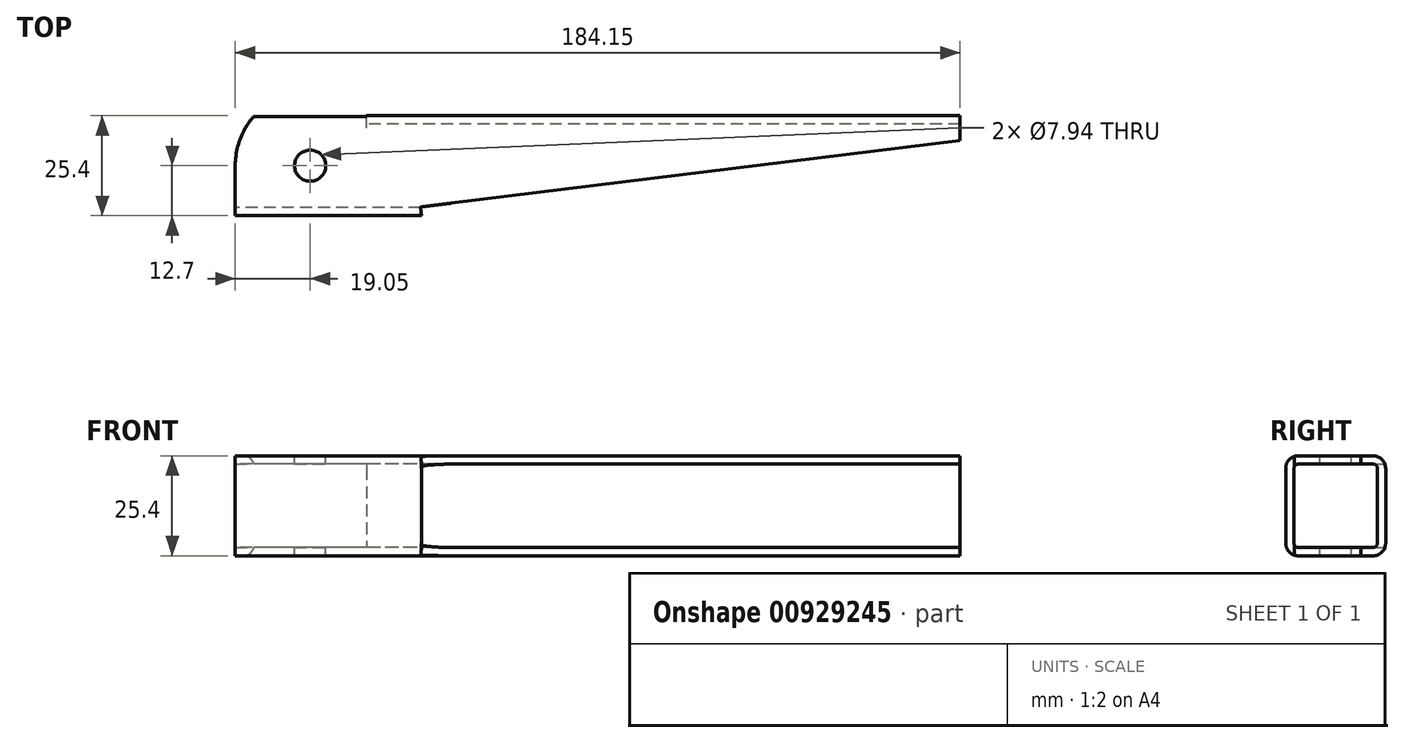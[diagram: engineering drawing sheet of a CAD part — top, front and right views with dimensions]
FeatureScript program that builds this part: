
annotation { "Feature Type Name" : "Feature", "Feature Type Description" : "" }
export const myFeature = defineFeature(function(context is Context, id is Id, definition is map)
    precondition{}
    {
        {
            var Q0;
            Q0=qCreatedBy(makeId("Right.planeOp"),FACE);
            var sketch = newSketch(context, id + "F0", { "sketchPlane" : qUnion([Q0])});
            skLineSegment(sketch, "E0.bottom", {"start": v(9.53, -12.7) * mm, "end": v(-9.53, -12.7) * mm});
            skLineSegment(sketch, "E0.top", {"start": v(9.53, 12.7) * mm, "end": v(-9.52, 12.7) * mm});
            skLineSegment(sketch, "E0.left", {"start": v(12.7, -9.53) * mm, "end": v(12.7, 9.53) * mm});
            skLineSegment(sketch, "E0.right", {"start": v(-12.7, -9.53) * mm, "end": v(-12.7, 9.52) * mm});
            skPoint(sketch, "E0.middle", {"position": v(0, 0) * mm});
            skPoint(sketch, "E1.visualSharp", {"position": v(-12.7, 12.7) * mm});
            skArc(sketch, "E1.filletArc", {"start": v(-9.52, 12.7) * mm, "mid": v(-11.77, 11.77) * mm, "end": v(-12.7, 9.52) * mm});
            skPoint(sketch, "E2.visualSharp", {"position": v(12.7, 12.7) * mm});
            skArc(sketch, "E2.filletArc", {"start": v(12.7, 9.53) * mm, "mid": v(11.77, 11.77) * mm, "end": v(9.53, 12.7) * mm});
            skPoint(sketch, "E3.visualSharp", {"position": v(12.7, -12.7) * mm});
            skArc(sketch, "E3.filletArc", {"start": v(9.53, -12.7) * mm, "mid": v(11.77, -11.77) * mm, "end": v(12.7, -9.53) * mm});
            skPoint(sketch, "E4.visualSharp", {"position": v(-12.7, -12.7) * mm});
            skArc(sketch, "E4.filletArc", {"start": v(-12.7, -9.53) * mm, "mid": v(-11.77, -11.77) * mm, "end": v(-9.53, -12.7) * mm});
            skLineSegment(sketch, "E5.0", {"start": v(9.53, 10.6) * mm, "end": v(-9.53, 10.6) * mm});
            skArc(sketch, "E5.1", {"start": v(10.6, 9.53) * mm, "mid": v(10.28, 10.28) * mm, "end": v(9.53, 10.6) * mm});
            skArc(sketch, "E5.2", {"start": v(-9.53, 10.6) * mm, "mid": v(-10.28, 10.28) * mm, "end": v(-10.6, 9.52) * mm});
            skLineSegment(sketch, "E5.3", {"start": v(10.6, -9.52) * mm, "end": v(10.6, 9.53) * mm});
            skLineSegment(sketch, "E5.4", {"start": v(-10.6, -9.53) * mm, "end": v(-10.6, 9.52) * mm});
            skArc(sketch, "E5.5", {"start": v(-10.6, -9.53) * mm, "mid": v(-10.28, -10.28) * mm, "end": v(-9.52, -10.6) * mm});
            skLineSegment(sketch, "E5.6", {"start": v(9.53, -10.6) * mm, "end": v(-9.52, -10.6) * mm});
            skArc(sketch, "E5.7", {"start": v(9.53, -10.6) * mm, "mid": v(10.28, -10.28) * mm, "end": v(10.6, -9.52) * mm});
            skSolve(sketch);
        }
        {
            var Q0;
            Q0=makeQuery(id+"F0.imprint","IMPRINT",FACE,{"disambiguationData":[TD([[makeQuery(id+"F0.imprint","IMPRINT",EDGE,{"derivedFrom":sQuery(id+"F0.wireOp",EDGE,"E0.bottom")}),-1.0]])]});
            extrude(context, id + "F1", {"entities" : qUnion([Q0]), "depth" : 184.15 * mm, "offsetDistance" : 25.4 * mm});
        }
        {
            var Q0;
            Q0=makeQuery(id+"F1.opExtrude","CAP_FACE",FACE,{"disambiguationData":[OSD([sQuery(id+"F0.wireOp",EDGE,"E0.bottom"),sQuery(id+"F0.wireOp",EDGE,"E0.top"),sQuery(id+"F0.wireOp",EDGE,"E0.left"),sQuery(id+"F0.wireOp",EDGE,"E0.right"),sQuery(id+"F0.wireOp",EDGE,"E1.filletArc"),sQuery(id+"F0.wireOp",EDGE,"E2.filletArc"),sQuery(id+"F0.wireOp",EDGE,"E3.filletArc"),sQuery(id+"F0.wireOp",EDGE,"E4.filletArc"),sQuery(id+"F0.wireOp",EDGE,"E5.0"),sQuery(id+"F0.wireOp",EDGE,"E5.1"),sQuery(id+"F0.wireOp",EDGE,"E5.2"),sQuery(id+"F0.wireOp",EDGE,"E5.3"),sQuery(id+"F0.wireOp",EDGE,"E5.4"),sQuery(id+"F0.wireOp",EDGE,"E5.5"),sQuery(id+"F0.wireOp",EDGE,"E5.6"),sQuery(id+"F0.wireOp",EDGE,"E5.7")])],"isStart":true});
            var sketch = newSketch(context, id + "F2", { "sketchPlane" : qUnion([Q0])});
            skLineSegment(sketch, "E6.bottom", {"start": v(-7.52, 10.6) * mm, "end": v(-16.03, 10.6) * mm});
            skLineSegment(sketch, "E6.top", {"start": v(-7.52, -10.6) * mm, "end": v(-16.03, -10.6) * mm});
            skLineSegment(sketch, "E6.left", {"start": v(-7.52, 10.6) * mm, "end": v(-7.52, -10.6) * mm});
            skLineSegment(sketch, "E6.right", {"start": v(-16.03, 10.6) * mm, "end": v(-16.03, -10.6) * mm});
            skSolve(sketch);
        }
        {
            var Q0;
            {var subQ1=sQuery(id+"F2.wireOp",EDGE,"E6.right");Q0=makeQuery(id+"F2.imprint","IMPRINT",FACE,{"disambiguationData":[TD([[makeQuery(id+"F2.imprint","IMPRINT",EDGE,{"derivedFrom":subQ1}),1.0]])]});}
            var Q1;
            {var subQ0=sQuery(id+"F2.wireOp",EDGE,"E6.left");Q1=makeQuery(id+"F2.imprint","IMPRINT",FACE,{"disambiguationData":[TD([[makeQuery(id+"F2.imprint","IMPRINT",EDGE,{"derivedFrom":subQ0}),-1.0]])]});}
            var Q2;
            {var subQ1=makeQuery(id+"F1.opExtrude","CAP_EDGE",EDGE,{"disambiguationData":[OSD([sQuery(id+"F0.wireOp",EDGE,"E0.left")])],"isStart":true});Q2=makeQuery(id+"F2.imprint","IMPRINT",FACE,{"disambiguationData":[TD([[makeQuery(id+"F2.imprint","IMPRINT",EDGE,{"derivedFrom":subQ1}),-1.0]])]});}
            extrude(context, id + "F3", {"entities" : qUnion([Q0, Q1, Q2]), "operationType" : NewBodyOperationType.REMOVE, "oppositeDirection" : true, "depth" : 33.34 * mm, "offsetDistance" : 25.4 * mm});
        }
        {
            var Q0;
            Q0=makeQuery(id+"F1.opExtrude","SWEPT_FACE",FACE,{"disambiguationData":[OSD([sQuery(id+"F0.wireOp",EDGE,"E0.top")])]});
            var sketch = newSketch(context, id + "F4", { "sketchPlane" : qUnion([Q0])});
            skCircle(sketch, "E7", {"center": v(19.05, 0) * mm, "radius": 3.97 * mm});
            skSolve(sketch);
        }
        {
            var Q0;
            Q0=makeQuery(id+"F4.imprint","IMPRINT",FACE,{"disambiguationData":[TD([[makeQuery(id+"F4.imprint","IMPRINT",EDGE,{"derivedFrom":sQuery(id+"F4.wireOp",EDGE,"E7")}),1.0]])]});
            extrude(context, id + "F5", {"entities" : qUnion([Q0]), "operationType" : NewBodyOperationType.REMOVE, "endBound" : BoundingType.THROUGH_ALL, "oppositeDirection" : true, "depth" : 25.4 * mm, "offsetDistance" : 25.4 * mm});
        }
        {
            var Q0;
            Q0=makeQuery(id+"F1.opExtrude","SWEPT_FACE",FACE,{"disambiguationData":[OSD([sQuery(id+"F0.wireOp",EDGE,"E0.top")])]});
            var sketch = newSketch(context, id + "F6", { "sketchPlane" : qUnion([Q0])});
            skArc(sketch, "E8", {"start": v(6.23, 14.09) * mm, "mid": v(1.63, 7.7) * mm, "end": v(0, 0) * mm});
            skArc(sketch, "E9", {"start": v(1.4, 20.38) * mm, "mid": v(-5.47, 11.2) * mm, "end": v(-7.9, 0) * mm});
            skLineSegment(sketch, "E10", {"start": v(-7.9, 0) * mm, "end": v(0, 0) * mm});
            skPoint(sketch, "E10.startSnap0", {"position": v(0, 0) * mm});
            skLineSegment(sketch, "E11", {"start": v(6.23, 14.09) * mm, "end": v(1.4, 20.38) * mm});
            skSolve(sketch);
        }
        {
            var Q0;
            Q0=makeQuery(id+"F6.imprint","IMPRINT",FACE,{"disambiguationData":[TD([[makeQuery(id+"F6.imprint","IMPRINT",EDGE,{"derivedFrom":sQuery(id+"F6.wireOp",EDGE,"E9")}),1.0]])]});
            var Q1;
            {var subQ0=sQuery(id+"F6.wireOp",EDGE,"E8");var subQ1=sQuery(id+"F0.wireOp",EDGE,"E0.top");var subQ2=makeQuery(id+"F1.opExtrude","CAP_EDGE",EDGE,{"disambiguationData":[OSD([subQ1])],"isStart":true});var subQ3=makeQuery(id+"F6.imprint","INTERSECT",VERTEX,{"derivedFrom":[subQ2,subQ0,sQuery(id+"F6.wireOp",EDGE,"E10")]});Q1=makeQuery(id+"F6.imprint","IMPRINT",FACE,{"disambiguationData":[TD([[makeQuery(id+"F6.imprint","IMPRINT",EDGE,{"disambiguationData":[TD([[subQ3,1.0]])],"derivedFrom":subQ0}),-1.0]])]});}
            extrude(context, id + "F7", {"entities" : qUnion([Q0, Q1]), "operationType" : NewBodyOperationType.REMOVE, "endBound" : BoundingType.THROUGH_ALL, "oppositeDirection" : true, "depth" : 25.4 * mm, "offsetDistance" : 25.4 * mm});
        }
        {
            var Q0;
            Q0=makeQuery(id+"F1.opExtrude","SWEPT_FACE",FACE,{"disambiguationData":[OSD([sQuery(id+"F0.wireOp",EDGE,"E0.top")])]});
            var sketch = newSketch(context, id + "F8", { "sketchPlane" : qUnion([Q0])});
            skLineSegment(sketch, "E12.bottom", {"start": v(184.15, 6.35) * mm, "end": v(47.07, -10.48) * mm});
            skLineSegment(sketch, "E12.top", {"start": v(188.56, -29.58) * mm, "end": v(51.48, -46.41) * mm});
            skLineSegment(sketch, "E12.left", {"start": v(184.15, 6.35) * mm, "end": v(188.56, -29.58) * mm});
            skLineSegment(sketch, "E12.right", {"start": v(47.07, -10.48) * mm, "end": v(51.48, -46.41) * mm});
            skSolve(sketch);
        }
        {
            var Q0;
            {var subQ0=sQuery(id+"F8.wireOp",EDGE,"E12.bottom");var subQ1=sQuery(id+"F0.wireOp",EDGE,"E0.top");var subQ2=makeQuery(id+"F1.opExtrude","CAP_EDGE",EDGE,{"disambiguationData":[OSD([subQ1])],"isStart":false});var subQ3=makeQuery(id+"F8.imprint","INTERSECT",VERTEX,{"derivedFrom":[subQ2,subQ0,sQuery(id+"F8.wireOp",EDGE,"E12.left")]});Q0=makeQuery(id+"F8.imprint","IMPRINT",FACE,{"disambiguationData":[TD([[makeQuery(id+"F8.imprint","IMPRINT",EDGE,{"disambiguationData":[TD([[subQ3,-1.0]])],"derivedFrom":subQ0}),1.0]])]});}
            var Q1;
            Q1=makeQuery(id+"F8.imprint","IMPRINT",FACE,{"disambiguationData":[TD([[makeQuery(id+"F8.imprint","IMPRINT",EDGE,{"derivedFrom":sQuery(id+"F8.wireOp",EDGE,"E12.top")}),-1.0]])]});
            extrude(context, id + "F9", {"entities" : qUnion([Q0, Q1]), "operationType" : NewBodyOperationType.REMOVE, "endBound" : BoundingType.THROUGH_ALL, "oppositeDirection" : true, "depth" : 25.4 * mm, "offsetDistance" : 25.4 * mm});
        }
    });
